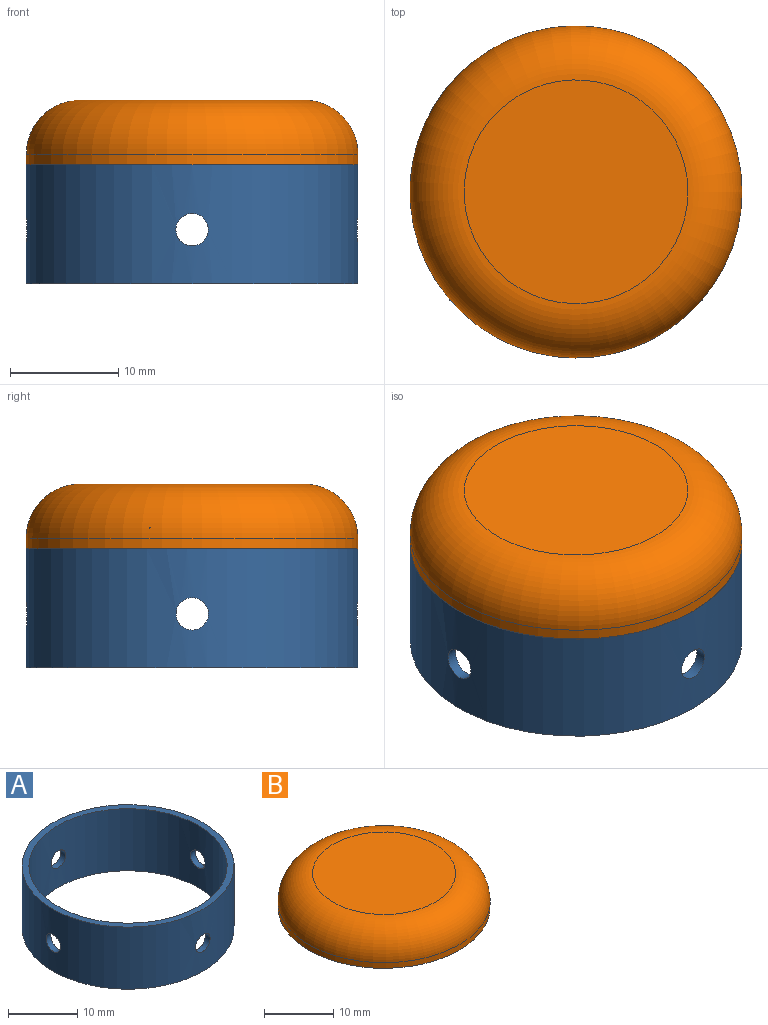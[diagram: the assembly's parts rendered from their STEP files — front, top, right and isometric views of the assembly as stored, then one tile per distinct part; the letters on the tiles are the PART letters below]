
ASSEMBLY  parts=2 mates=1
PART A: 8 faces, bbox 30.7x30.7x11 mm
  f0: cylinder r=14.35mm len=28.7mm, axis (0,0,-1), area 963.5mm2, adj f2,f3,f4,f5,f6,f7
  f1: cylinder r=15.35mm len=30.7mm, axis (0,0,-1), area 1032.6mm2, adj f2,f3,f4,f5,f6,f7
  f2: plane 30.7x30.7mm, normal (0,0,1), area 93.3mm2, adj f0,f1
  f3: plane 30.7x30.7mm, normal (0,0,-1), area 93.3mm2, adj f0,f1
  f4: cylinder r=1.5mm len=3mm, axis (1,0,0), area 9.4mm2, adj f0,f1
  f5: cylinder r=1.5mm len=3mm, axis (1,0,0), area 9.4mm2, adj f0,f1
  f6: cylinder r=1.5mm len=3mm, axis (0,-1,0), area 9.4mm2, adj f0,f1
  f7: cylinder r=1.5mm len=3mm, axis (0,-1,0), area 9.4mm2, adj f0,f1
PART B: 88 faces, bbox 33.2x33.2x6 mm
  f0: plane 30.7x30.7mm, normal (0,0,-1), area 362.2mm2, adj f1,f3,f4,f5,f6,f7,f8,f10
  f1: cylinder r=15.35mm len=30.7mm, axis (0,0,1), area 96.4mm2, adj f0,f87
  f2: plane 20.7x20.7mm, normal (0,0,1), area 336.5mm2, adj f87
  f3: plane 3.35x2mm, normal (1,0,0), area 6.7mm2, adj f0,f4,f8,f9
  f4: plane 2.91x2mm, normal (0.5,0.87,0), area 6.7mm2, adj f0,f3,f5,f9
  f5: plane 3.02x2mm, normal (-0.5,0.87,0), area 7mm2, adj f0,f4,f6,f9
  f6: plane 3.35x2mm, normal (-1,0,0), area 6.7mm2, adj f0,f5,f7,f9
  f7: plane 2.91x2mm, normal (-0.5,-0.87,0), area 6.7mm2, adj f0,f6,f8,f9
  f8: plane 3.02x2mm, normal (0.5,-0.87,0), area 7mm2, adj f0,f3,f7,f9
  f9: plane 6.77x5.93mm, normal (0,0,-1), area 30mm2, adj f3,f4,f5,f6,f7,f8
  f10: plane 3.02x2mm, normal (-0.5,0.87,0), area 7mm2, adj f0,f11,f15,f16
  f11: plane 3.49x2mm, normal (-1,0,0), area 7mm2, adj f0,f10,f12,f16
  f12: plane 3.02x2mm, normal (-0.5,-0.87,0), area 7mm2, adj f0,f11,f13,f16
  f13: plane 3.02x2mm, normal (0.5,-0.87,0), area 7mm2, adj f0,f12,f14,f16
  f14: plane 3.49x2mm, normal (1,0,0), area 7mm2, adj f0,f13,f15,f16
  f15: plane 3.02x2mm, normal (0.5,0.87,0), area 7mm2, adj f0,f10,f14,f16
  f16: plane 6.98x6.04mm, normal (0,0,-1), area 31.6mm2, adj f10,f11,f12,f13,f14,f15
  f17: plane 3.02x2mm, normal (0.5,0.87,0), area 7mm2, adj f0,f18,f22,f23
  f18: plane 3.02x2mm, normal (-0.5,0.87,0), area 7mm2, adj f0,f17,f19,f23
  f19: plane 3.49x2mm, normal (-1,0,0), area 7mm2, adj f0,f18,f20,f23
  f20: plane 3.02x2mm, normal (-0.5,-0.87,0), area 7mm2, adj f0,f19,f21,f23
  f21: plane 3.02x2mm, normal (0.5,-0.87,0), area 7mm2, adj f0,f20,f22,f23
  f22: plane 3.49x2mm, normal (1,0,0), area 7mm2, adj f0,f17,f21,f23
  f23: plane 6.98x6.04mm, normal (0,0,-1), area 31.6mm2, adj f17,f18,f19,f20,f21,f22
  f24: plane 3.02x2mm, normal (0.5,0.87,0), area 7mm2, adj f0,f25,f29,f30
  f25: plane 3.02x2mm, normal (-0.5,0.87,0), area 7mm2, adj f0,f24,f26,f30
  f26: plane 3.49x2mm, normal (-1,0,0), area 7mm2, adj f0,f25,f27,f30
  f27: plane 3.02x2mm, normal (-0.5,-0.87,0), area 7mm2, adj f0,f26,f28,f30
  f28: plane 3.02x2mm, normal (0.5,-0.87,0), area 7mm2, adj f0,f27,f29,f30
  f29: plane 3.49x2mm, normal (1,0,0), area 7mm2, adj f0,f24,f28,f30
  f30: plane 6.98x6.04mm, normal (0,0,-1), area 31.6mm2, adj f24,f25,f26,f27,f28,f29
  f31: plane 3.49x2mm, normal (-1,0,0), area 7mm2, adj f0,f32,f36,f37
  f32: plane 3.02x2mm, normal (-0.5,-0.87,0), area 7mm2, adj f0,f31,f33,f37
  f33: plane 3.02x2mm, normal (0.5,-0.87,0), area 7mm2, adj f0,f32,f34,f37
  f34: plane 3.49x2mm, normal (1,0,0), area 7mm2, adj f0,f33,f35,f37
  f35: plane 3.02x2mm, normal (0.5,0.87,0), area 7mm2, adj f0,f34,f36,f37
  f36: plane 3.02x2mm, normal (-0.5,0.87,0), area 7mm2, adj f0,f31,f35,f37
  f37: plane 6.98x6.04mm, normal (0,0,-1), area 31.6mm2, adj f31,f32,f33,f34,f35,f36
  f38: plane 3.02x2mm, normal (0.5,0.87,0), area 7mm2, adj f0,f39,f43,f44
  f39: plane 3.02x2mm, normal (-0.5,0.87,0), area 7mm2, adj f0,f38,f40,f44
  f40: plane 3.49x2mm, normal (-1,0,0), area 7mm2, adj f0,f39,f41,f44
  f41: plane 3.02x2mm, normal (-0.5,-0.87,0), area 7mm2, adj f0,f40,f42,f44
  f42: plane 3.02x2mm, normal (0.5,-0.87,0), area 7mm2, adj f0,f41,f43,f44
  f43: plane 3.49x2mm, normal (1,0,0), area 7mm2, adj f0,f38,f42,f44
  f44: plane 6.98x6.04mm, normal (0,0,-1), area 31.6mm2, adj f38,f39,f40,f41,f42,f43
  f45: plane 3.02x2mm, normal (0.5,0.87,0), area 7mm2, adj f0,f46,f50,f51
  f46: plane 3.02x2mm, normal (-0.5,0.87,0), area 7mm2, adj f0,f45,f47,f51
  f47: plane 3.49x2mm, normal (-1,0,0), area 7mm2, adj f0,f46,f48,f51
  f48: plane 3.02x2mm, normal (-0.5,-0.87,0), area 7mm2, adj f0,f47,f49,f51
  f49: plane 3.02x2mm, normal (0.5,-0.87,0), area 7mm2, adj f0,f48,f50,f51
  f50: plane 3.49x2mm, normal (1,0,0), area 7mm2, adj f0,f45,f49,f51
  f51: plane 6.98x6.04mm, normal (0,0,-1), area 31.6mm2, adj f45,f46,f47,f48,f49,f50
  f52: plane 3.02x2mm, normal (0.5,0.87,0), area 7mm2, adj f0,f53,f57,f58
  f53: plane 3.02x2mm, normal (-0.5,0.87,0), area 7mm2, adj f0,f52,f54,f58
  f54: plane 3.49x2mm, normal (-1,0,0), area 7mm2, adj f0,f53,f55,f58
  f55: plane 3.02x2mm, normal (-0.5,-0.87,0), area 7mm2, adj f0,f54,f56,f58
  f56: plane 3.02x2mm, normal (0.5,-0.87,0), area 7mm2, adj f0,f55,f57,f58
  f57: plane 3.49x2mm, normal (1,0,0), area 7mm2, adj f0,f52,f56,f58
  f58: plane 6.98x6.04mm, normal (0,0,-1), area 31.6mm2, adj f52,f53,f54,f55,f56,f57
  f59: plane 3.02x2mm, normal (0.5,0.87,0), area 7mm2, adj f0,f60,f64,f65
  f60: plane 3.02x2mm, normal (-0.5,0.87,0), area 7mm2, adj f0,f59,f61,f65
  f61: plane 3.49x2mm, normal (-1,0,0), area 7mm2, adj f0,f60,f62,f65
  f62: plane 3.02x2mm, normal (-0.5,-0.87,0), area 7mm2, adj f0,f61,f63,f65
  f63: plane 3.02x2mm, normal (0.5,-0.87,0), area 7mm2, adj f0,f62,f64,f65
  f64: plane 3.49x2mm, normal (1,0,0), area 7mm2, adj f0,f59,f63,f65
  f65: plane 6.98x6.04mm, normal (0,0,-1), area 31.6mm2, adj f59,f60,f61,f62,f63,f64
  f66: plane 3.02x2mm, normal (0.5,0.87,0), area 7mm2, adj f0,f67,f71,f72
  f67: plane 3.02x2mm, normal (-0.5,0.87,0), area 7mm2, adj f0,f66,f68,f72
  f68: plane 3.49x2mm, normal (-1,0,0), area 7mm2, adj f0,f67,f69,f72
  f69: plane 3.02x2mm, normal (-0.5,-0.87,0), area 7mm2, adj f0,f68,f70,f72
  f70: plane 3.02x2mm, normal (0.5,-0.87,0), area 7mm2, adj f0,f69,f71,f72
  f71: plane 3.49x2mm, normal (1,0,0), area 7mm2, adj f0,f66,f70,f72
  f72: plane 6.98x6.04mm, normal (0,0,-1), area 31.6mm2, adj f66,f67,f68,f69,f70,f71
  f73: plane 3.02x2mm, normal (0.5,0.87,0), area 7mm2, adj f0,f74,f78,f79
  f74: plane 3.02x2mm, normal (-0.5,0.87,0), area 7mm2, adj f0,f73,f75,f79
  f75: plane 3.49x2mm, normal (-1,0,0), area 7mm2, adj f0,f74,f76,f79
  f76: plane 3.02x2mm, normal (-0.5,-0.87,0), area 7mm2, adj f0,f75,f77,f79
  f77: plane 3.02x2mm, normal (0.5,-0.87,0), area 7mm2, adj f0,f76,f78,f79
  f78: plane 3.49x2mm, normal (1,0,0), area 7mm2, adj f0,f73,f77,f79
  f79: plane 6.98x6.04mm, normal (0,0,-1), area 31.6mm2, adj f73,f74,f75,f76,f77,f78
  f80: plane 3.02x2mm, normal (0.5,0.87,0), area 7mm2, adj f0,f81,f85,f86
  f81: plane 3.02x2mm, normal (-0.5,0.87,0), area 7mm2, adj f0,f80,f82,f86
  f82: plane 3.49x2mm, normal (-1,0,0), area 7mm2, adj f0,f81,f83,f86
  f83: plane 3.02x2mm, normal (-0.5,-0.87,0), area 7mm2, adj f0,f82,f84,f86
  f84: plane 3.02x2mm, normal (0.5,-0.87,0), area 7mm2, adj f0,f83,f85,f86
  f85: plane 3.49x2mm, normal (1,0,0), area 7mm2, adj f0,f80,f84,f86
  f86: plane 6.98x6.04mm, normal (0,0,-1), area 31.6mm2, adj f80,f81,f82,f83,f84,f85
  f87: torus R=10.35mm, axis (0,0,1), area 667.8mm2, adj f1,f2
PLACE A rot(axis=(0,0,-1),90deg) t=(-9.91,-0.48,-16.14)mm
PLACE B t=(-9.91,-0.48,0.86)mm
MATE fastened A.f1 <-> B.f1  axis (0,0,1) through (-9.91,-0.48,-5.14)mm
